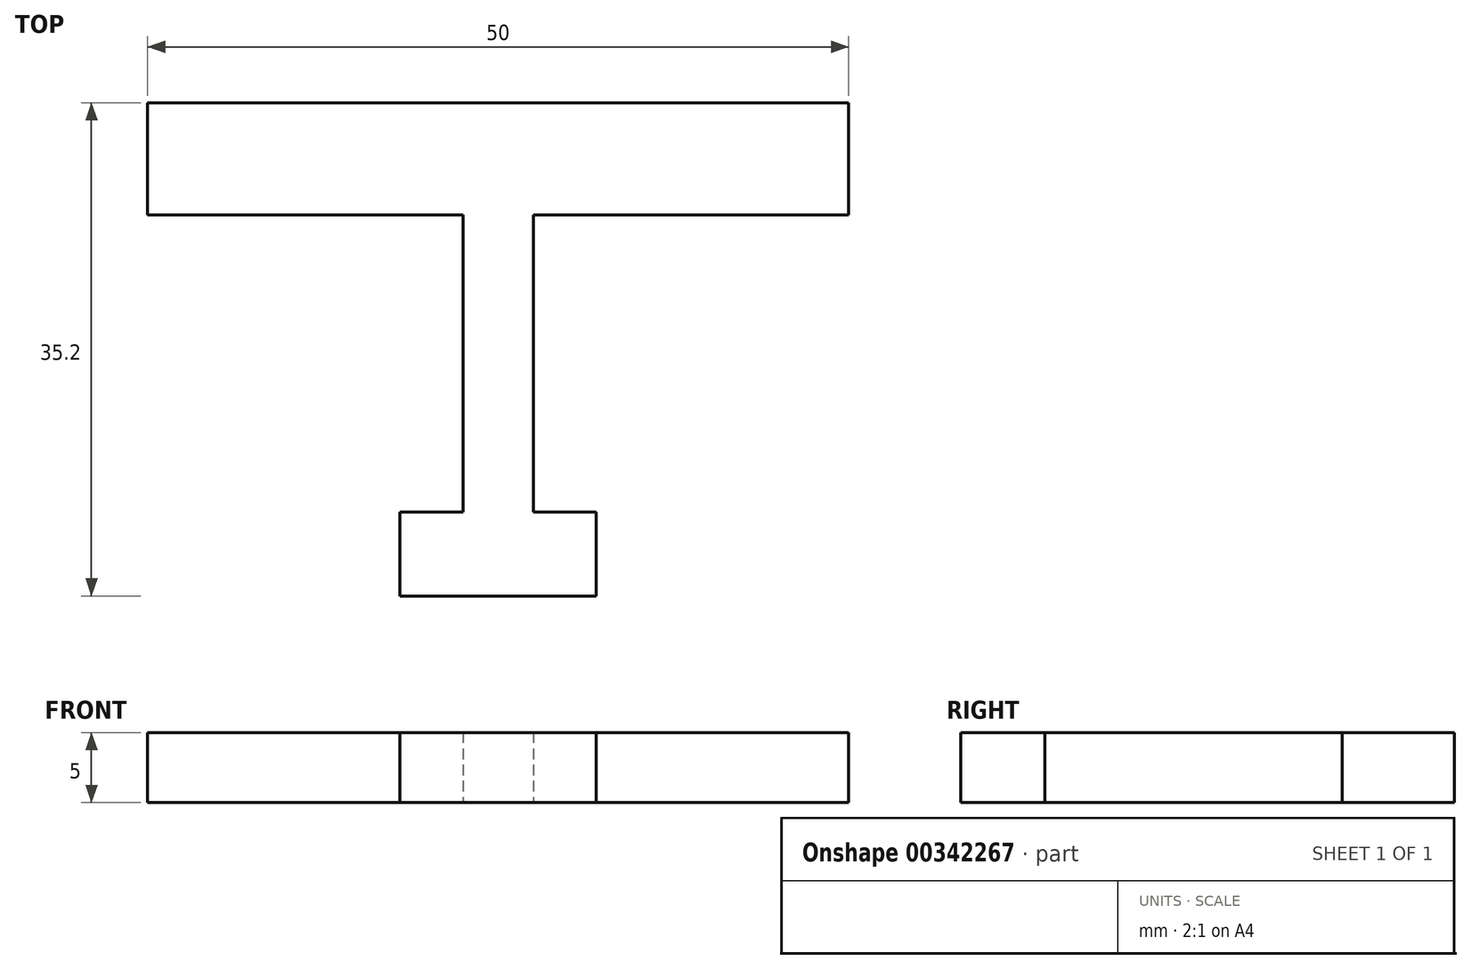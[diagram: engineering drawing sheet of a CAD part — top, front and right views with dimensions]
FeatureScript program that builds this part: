
annotation { "Feature Type Name" : "Feature", "Feature Type Description" : "" }
export const myFeature = defineFeature(function(context is Context, id is Id, definition is map)
    precondition{}
    {
        {
            var Q0;
            Q0=qCreatedBy(makeId("Top.planeOp"),FACE);
            var sketch = newSketch(context, id + "F0", { "sketchPlane" : qUnion([Q0])});
            skLineSegment(sketch, "E0", {"start": v(-23.7, 26.12) * mm, "end": v(-23.7, 18.12) * mm});
            skLineSegment(sketch, "E1", {"start": v(-23.7, 18.12) * mm, "end": v(-1.2, 18.12) * mm});
            skLineSegment(sketch, "E2", {"start": v(-1.2, 18.12) * mm, "end": v(-1.2, -3.08) * mm});
            skLineSegment(sketch, "E3", {"start": v(-1.2, -3.08) * mm, "end": v(-5.7, -3.08) * mm});
            skLineSegment(sketch, "E4", {"start": v(-5.7, -3.08) * mm, "end": v(-5.7, -9.08) * mm});
            skLineSegment(sketch, "E5", {"start": v(-5.7, -9.08) * mm, "end": v(8.3, -9.08) * mm});
            skLineSegment(sketch, "E6", {"start": v(8.3, -9.08) * mm, "end": v(8.3, -3.08) * mm});
            skLineSegment(sketch, "E7", {"start": v(8.3, -3.08) * mm, "end": v(3.8, -3.08) * mm});
            skLineSegment(sketch, "E8", {"start": v(3.8, -3.08) * mm, "end": v(3.8, 18.12) * mm});
            skLineSegment(sketch, "E9", {"start": v(3.8, 18.12) * mm, "end": v(26.3, 18.12) * mm});
            skLineSegment(sketch, "E10", {"start": v(26.3, 18.12) * mm, "end": v(26.3, 26.12) * mm});
            skLineSegment(sketch, "E11", {"start": v(26.3, 26.12) * mm, "end": v(-23.7, 26.12) * mm});
            skSolve(sketch);
        }
        {
            var Q0;
            {var subQ5=sQuery(id+"F0.wireOp",EDGE,"E0");Q0=makeQuery(id+"F0.imprint","IMPRINT",FACE,{"disambiguationData":[TD([[makeQuery(id+"F0.imprint","IMPRINT",EDGE,{"derivedFrom":subQ5}),1.0]])]});}
            extrude(context, id + "F1", {"entities" : qUnion([Q0]), "depth" : 5 * mm});
        }
    });
